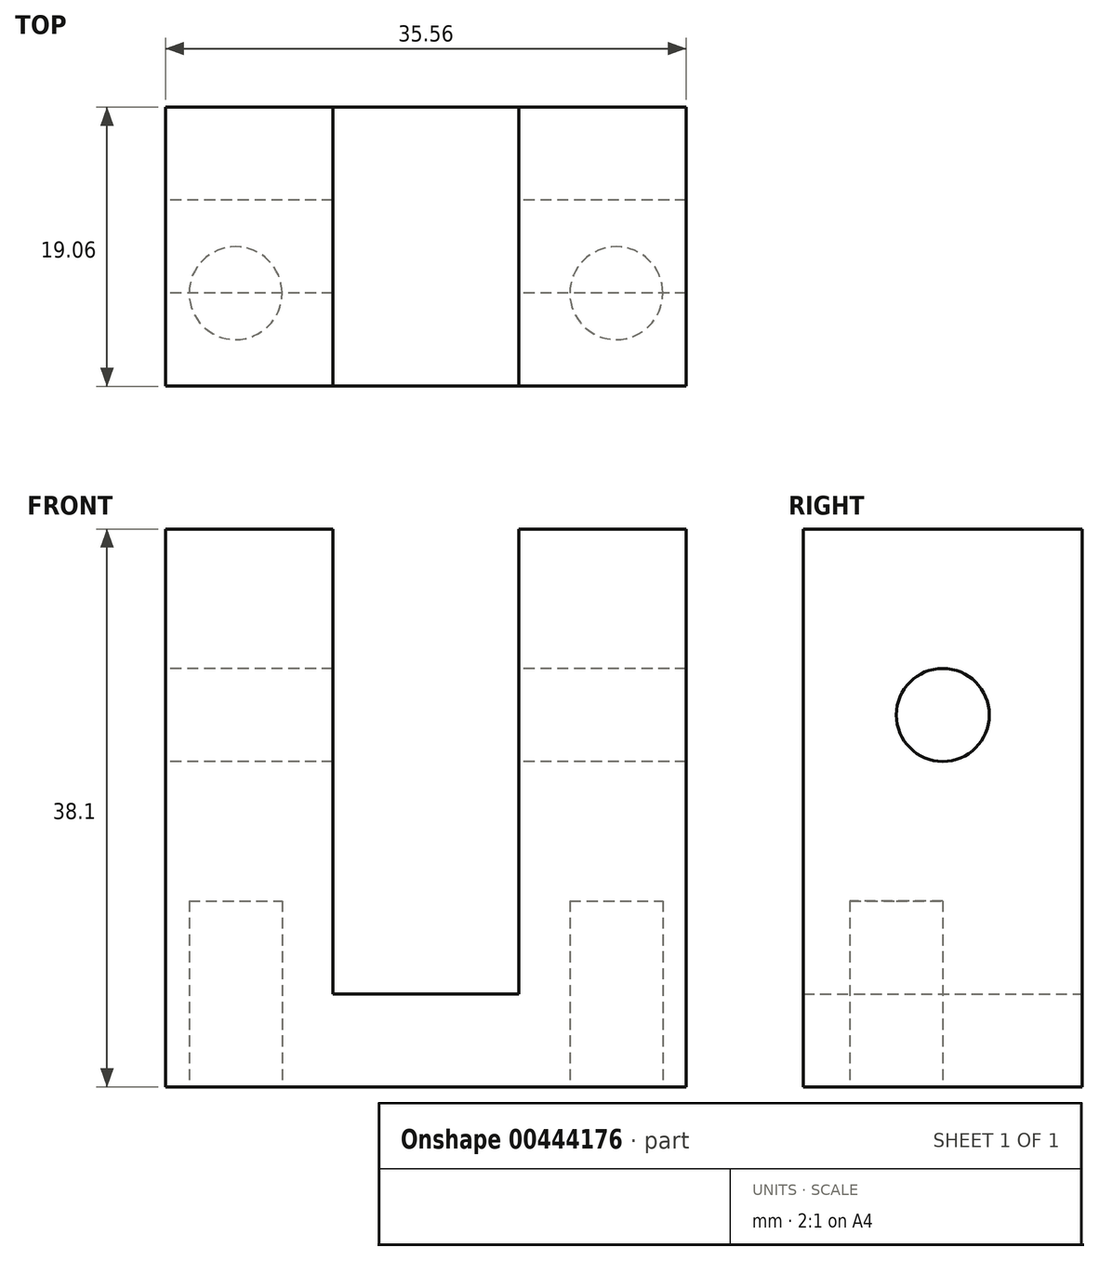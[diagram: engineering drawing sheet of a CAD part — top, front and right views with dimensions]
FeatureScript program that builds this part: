
annotation { "Feature Type Name" : "Feature", "Feature Type Description" : "" }
export const myFeature = defineFeature(function(context is Context, id is Id, definition is map)
    precondition{}
    {
        {
            var Q0;
            Q0=qCreatedBy(makeId("Front.planeOp"),FACE);
            var sketch = newSketch(context, id + "F0", { "sketchPlane" : qUnion([Q0])});
            skLineSegment(sketch, "E0.bottom", {"start": v(-17.78, 12.7) * mm, "end": v(-6.35, 12.7) * mm});
            skLineSegment(sketch, "E0.top", {"start": v(-17.78, -25.4) * mm, "end": v(17.78, -25.4) * mm});
            skLineSegment(sketch, "E0.left", {"start": v(-17.78, 12.7) * mm, "end": v(-17.78, -25.4) * mm});
            skLineSegment(sketch, "E0.right", {"start": v(17.78, 12.7) * mm, "end": v(17.78, -25.4) * mm});
            skLineSegment(sketch, "E1.top", {"start": v(-6.35, -19.05) * mm, "end": v(6.35, -19.05) * mm});
            skLineSegment(sketch, "E1.left", {"start": v(-6.35, 12.7) * mm, "end": v(-6.35, -19.05) * mm});
            skLineSegment(sketch, "E1.right", {"start": v(6.35, 12.7) * mm, "end": v(6.35, -19.05) * mm});
            skLineSegment(sketch, "E2.trimOffspring", {"start": v(6.35, 12.7) * mm, "end": v(17.78, 12.7) * mm});
            skSolve(sketch);
        }
        {
            var Q0;
            Q0 = qSketchRegion(id + "F0", true);
            extrude(context, id + "F1", {"entities" : qUnion([Q0]), "endBound" : BoundingType.SYMMETRIC, "depth" : 19.05 * mm});
        }
        {
            var Q0;
            Q0=makeQuery(id+"F1.opExtrude","SWEPT_FACE",FACE,{"disambiguationData":[OSD([sQuery(id+"F0.wireOp",EDGE,"E0.left")])]});
            var sketch = newSketch(context, id + "F2", { "sketchPlane" : qUnion([Q0])});
            skCircle(sketch, "E3", {"center": v(0, 0) * mm, "radius": 3.18 * mm});
            skSolve(sketch);
        }
        {
            var Q0;
            Q0 = qSketchRegion(id + "F2", true);
            extrude(context, id + "F3", {"entities" : qUnion([Q0]), "operationType" : NewBodyOperationType.REMOVE, "endBound" : BoundingType.THROUGH_ALL, "oppositeDirection" : true, "depth" : 25.4 * mm});
        }
        {
            var Q0;
            Q0=makeQuery(id+"F1.opExtrude","SWEPT_FACE",FACE,{"disambiguationData":[OSD([sQuery(id+"F0.wireOp",EDGE,"E0.top")])]});
            var sketch = newSketch(context, id + "F4", { "sketchPlane" : qUnion([Q0])});
            skCircle(sketch, "E4", {"center": v(-13, 3.17) * mm, "radius": 3.17 * mm});
            skCircle(sketch, "E5", {"center": v(13, 3.18) * mm, "radius": 3.17 * mm});
            skSolve(sketch);
        }
        {
            var Q0;
            Q0 = qSketchRegion(id + "F4", true);
            extrude(context, id + "F5", {"entities" : qUnion([Q0]), "operationType" : NewBodyOperationType.REMOVE, "oppositeDirection" : true, "depth" : 12.7 * mm});
        }
    });
